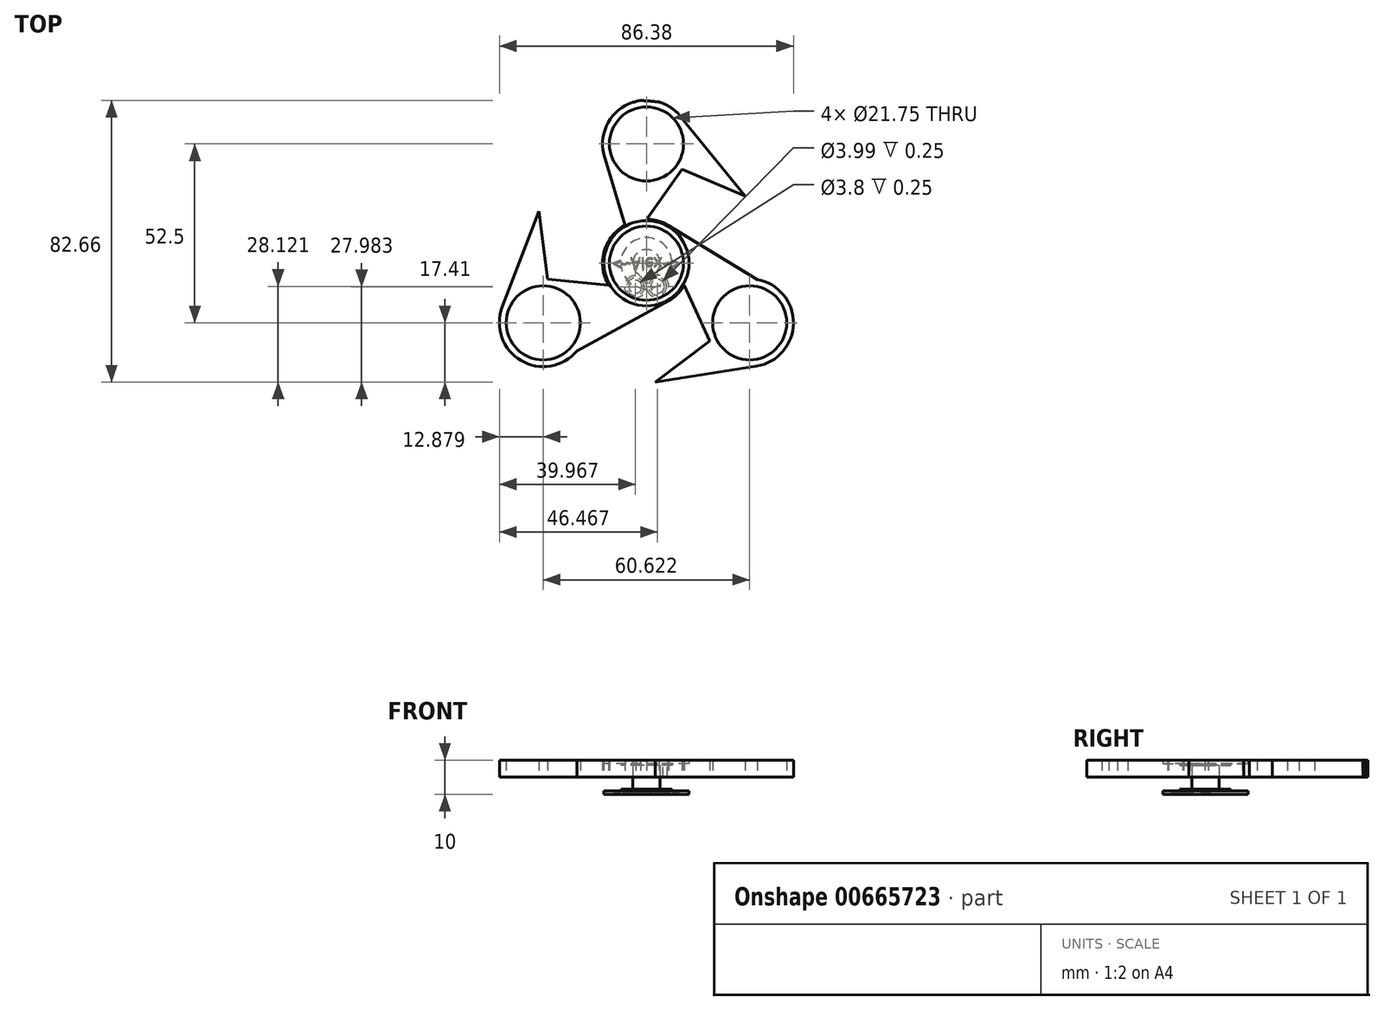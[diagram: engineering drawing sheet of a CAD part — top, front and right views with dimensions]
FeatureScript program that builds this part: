
annotation { "Feature Type Name" : "Feature", "Feature Type Description" : "" }
export const myFeature = defineFeature(function(context is Context, id is Id, definition is map)
    precondition{}
    {
        {
            var Q0;
            Q0=qCreatedBy(makeId("Top.planeOp"),FACE);
            var sketch = newSketch(context, id + "F0", { "sketchPlane" : qUnion([Q0])});
            skCircle(sketch, "E0", {"center": v(0, 0) * mm, "radius": 11.1 * mm});
            skCircle(sketch, "E1", {"center": v(0, 0) * mm, "radius": 4 * mm});
            skCircle(sketch, "E2.cCircle", {"center": v(0, 24.15) * mm, "radius": 6.8 * mm, "construction": true});
            skLineSegment(sketch, "E2.0", {"start": v(3.93, 17.35) * mm, "end": v(-3.93, 17.35) * mm});
            skLineSegment(sketch, "E2.1", {"start": v(-3.93, 17.35) * mm, "end": v(-7.85, 24.15) * mm});
            skLineSegment(sketch, "E2.2", {"start": v(-7.85, 24.15) * mm, "end": v(-3.93, 30.95) * mm});
            skLineSegment(sketch, "E2.3", {"start": v(-3.93, 30.95) * mm, "end": v(3.93, 30.95) * mm});
            skLineSegment(sketch, "E2.4", {"start": v(3.93, 30.95) * mm, "end": v(7.85, 24.15) * mm});
            skLineSegment(sketch, "E2.5", {"start": v(7.85, 24.15) * mm, "end": v(3.93, 17.35) * mm});
            skPoint(sketch, "E2.0.midPoint", {"position": v(0, 17.35) * mm});
            skLineSegment(sketch, "E3", {"start": v(0, 0) * mm, "end": v(0, 35) * mm, "construction": true});
            skArc(sketch, "E4", {"start": v(-11.18, 8.6) * mm, "mid": v(-12.21, 7.05) * mm, "end": v(-13.03, 5.38) * mm});
            skArc(sketch, "E5", {"start": v(-11.18, 8.6) * mm, "mid": v(-9, 13.96) * mm, "end": v(-9.89, 19.68) * mm});
            skArc(sketch, "E6", {"start": v(9.89, 19.68) * mm, "mid": v(9, 13.96) * mm, "end": v(11.18, 8.6) * mm});
            skArc(sketch, "E7.trimOffspring", {"start": v(9.89, 19.68) * mm, "mid": v(0, 35) * mm, "end": v(-9.89, 19.68) * mm});
            skArc(sketch, "E8.1.0", {"start": v(-1.86, -13.98) * mm, "mid": v(-7.59, -14.77) * mm, "end": v(-12.1, -18.4) * mm});
            skArc(sketch, "E8.1.1", {"start": v(-21.99, -1.28) * mm, "mid": v(-30.31, -17.5) * mm, "end": v(-12.1, -18.4) * mm});
            skLineSegment(sketch, "E8.1.2", {"start": v(-13.06, -12.07) * mm, "end": v(-16.99, -18.87) * mm});
            skLineSegment(sketch, "E8.1.3", {"start": v(-16.99, -18.87) * mm, "end": v(-24.84, -18.87) * mm});
            skLineSegment(sketch, "E8.1.4", {"start": v(-24.84, -18.87) * mm, "end": v(-28.76, -12.07) * mm});
            skLineSegment(sketch, "E8.1.5", {"start": v(-28.76, -12.07) * mm, "end": v(-24.84, -5.27) * mm});
            skLineSegment(sketch, "E8.1.6", {"start": v(-24.84, -5.27) * mm, "end": v(-16.99, -5.27) * mm});
            skLineSegment(sketch, "E8.1.7", {"start": v(-16.99, -5.27) * mm, "end": v(-13.06, -12.07) * mm});
            skArc(sketch, "E8.1.8", {"start": v(-21.99, -1.28) * mm, "mid": v(-16.59, 0.81) * mm, "end": v(-13.03, 5.38) * mm});
            skArc(sketch, "E8.2.0", {"start": v(13.03, 5.38) * mm, "mid": v(16.59, 0.81) * mm, "end": v(21.99, -1.28) * mm});
            skArc(sketch, "E8.2.1", {"start": v(12.1, -18.4) * mm, "mid": v(30.31, -17.5) * mm, "end": v(21.99, -1.28) * mm});
            skLineSegment(sketch, "E8.2.2", {"start": v(16.99, -5.27) * mm, "end": v(24.84, -5.27) * mm});
            skLineSegment(sketch, "E8.2.3", {"start": v(24.84, -5.27) * mm, "end": v(28.76, -12.07) * mm});
            skLineSegment(sketch, "E8.2.4", {"start": v(28.76, -12.07) * mm, "end": v(24.84, -18.87) * mm});
            skLineSegment(sketch, "E8.2.5", {"start": v(24.84, -18.87) * mm, "end": v(16.99, -18.87) * mm});
            skLineSegment(sketch, "E8.2.6", {"start": v(16.99, -18.87) * mm, "end": v(13.06, -12.07) * mm});
            skLineSegment(sketch, "E8.2.7", {"start": v(13.06, -12.07) * mm, "end": v(16.99, -5.27) * mm});
            skArc(sketch, "E8.2.8", {"start": v(12.1, -18.4) * mm, "mid": v(7.59, -14.77) * mm, "end": v(1.86, -13.98) * mm});
            skArc(sketch, "E9.trimOffspring", {"start": v(-1.86, -13.98) * mm, "mid": v(0, -14.1) * mm, "end": v(1.86, -13.98) * mm});
            skArc(sketch, "E10.trimOffspring", {"start": v(13.03, 5.38) * mm, "mid": v(12.21, 7.05) * mm, "end": v(11.18, 8.6) * mm});
            skArc(sketch, "E11", {"start": v(-13.03, 5.38) * mm, "mid": v(-14.09, 0.64) * mm, "end": v(-13.47, -4.18) * mm});
            skArc(sketch, "E12", {"start": v(11.18, 8.6) * mm, "mid": v(7.6, 11.88) * mm, "end": v(3.11, 13.75) * mm});
            skArc(sketch, "E13", {"start": v(1.86, -13.98) * mm, "mid": v(6.49, -12.52) * mm, "end": v(10.35, -9.57) * mm});
            skArc(sketch, "E14", {"start": v(-12.1, -18.4) * mm, "mid": v(-10.27, -14.18) * mm, "end": v(-10.35, -9.57) * mm});
            skArc(sketch, "E15", {"start": v(-9.89, 19.68) * mm, "mid": v(-7.14, 15.98) * mm, "end": v(-3.11, 13.75) * mm});
            skArc(sketch, "E16", {"start": v(21.99, -1.28) * mm, "mid": v(17.41, -1.8) * mm, "end": v(13.47, -4.18) * mm});
            skLineSegment(sketch, "E17", {"start": v(0, 24.15) * mm, "end": v(5.43, 33.55) * mm, "construction": true});
            skArc(sketch, "E18.trimOffspring", {"start": v(-13.47, -4.18) * mm, "mid": v(-17.41, -1.8) * mm, "end": v(-21.99, -1.28) * mm});
            skArc(sketch, "E19.trimOffspring", {"start": v(10.35, -9.57) * mm, "mid": v(10.27, -14.18) * mm, "end": v(12.1, -18.4) * mm});
            skArc(sketch, "E20.trimOffspring", {"start": v(3.11, 13.75) * mm, "mid": v(7.14, 15.98) * mm, "end": v(9.89, 19.68) * mm});
            skCircle(sketch, "E21", {"center": v(0, 0) * mm, "radius": 7.5 * mm});
            skCircle(sketch, "E22", {"center": v(0, 0) * mm, "radius": 12.5 * mm});
            skArc(sketch, "E23.trimOffspring", {"start": v(-3.11, 13.75) * mm, "mid": v(-7.6, 11.88) * mm, "end": v(-11.18, 8.6) * mm});
            skArc(sketch, "E24.trimOffspring", {"start": v(-10.35, -9.57) * mm, "mid": v(-6.49, -12.52) * mm, "end": v(-1.86, -13.98) * mm});
            skArc(sketch, "E25.trimOffspring", {"start": v(13.47, -4.18) * mm, "mid": v(14.09, 0.64) * mm, "end": v(13.03, 5.38) * mm});
            skSolve(sketch);
        }
        {
            var Q0;
            {var subQ1=sQuery(id+"F0.wireOp",EDGE,"E8.1.1");Q0=makeQuery(id+"F0.imprint","IMPRINT",FACE,{"disambiguationData":[TD([[makeQuery(id+"F0.imprint","IMPRINT",EDGE,{"derivedFrom":subQ1}),1.0]])]});}
            var Q1;
            {var subQ0=sQuery(id+"F0.wireOp",EDGE,"E8.1.8");Q1=makeQuery(id+"F0.imprint","IMPRINT",FACE,{"disambiguationData":[TD([[makeQuery(id+"F0.imprint","IMPRINT",EDGE,{"derivedFrom":subQ0}),-1.0]])]});}
            var Q2;
            Q2=makeQuery(id+"F0.imprint","IMPRINT",FACE,{"disambiguationData":[TD([[makeQuery(id+"F0.imprint","IMPRINT",EDGE,{"derivedFrom":sQuery(id+"F0.wireOp",EDGE,"E0")}),-1.0]])]});
            var Q3;
            {var subQ0=sQuery(id+"F0.wireOp",EDGE,"E5");Q3=makeQuery(id+"F0.imprint","IMPRINT",FACE,{"disambiguationData":[TD([[makeQuery(id+"F0.imprint","IMPRINT",EDGE,{"derivedFrom":subQ0}),-1.0]])]});}
            var Q4;
            Q4=makeQuery(id+"F0.imprint","IMPRINT",FACE,{"disambiguationData":[TD([[makeQuery(id+"F0.imprint","IMPRINT",EDGE,{"derivedFrom":sQuery(id+"F0.wireOp",EDGE,"E2.0")}),1.0]])]});
            var Q5;
            {var subQ0=sQuery(id+"F0.wireOp",EDGE,"E8.1.0");Q5=makeQuery(id+"F0.imprint","IMPRINT",FACE,{"disambiguationData":[TD([[makeQuery(id+"F0.imprint","IMPRINT",EDGE,{"derivedFrom":subQ0}),-1.0]])]});}
            var Q6;
            {var subQ0=sQuery(id+"F0.wireOp",EDGE,"E8.2.0");Q6=makeQuery(id+"F0.imprint","IMPRINT",FACE,{"disambiguationData":[TD([[makeQuery(id+"F0.imprint","IMPRINT",EDGE,{"derivedFrom":subQ0}),-1.0]])]});}
            var Q7;
            {var subQ0=sQuery(id+"F0.wireOp",EDGE,"E8.2.8");Q7=makeQuery(id+"F0.imprint","IMPRINT",FACE,{"disambiguationData":[TD([[makeQuery(id+"F0.imprint","IMPRINT",EDGE,{"derivedFrom":subQ0}),-1.0]])]});}
            var Q8;
            {var subQ0=sQuery(id+"F0.wireOp",EDGE,"E8.2.1");Q8=makeQuery(id+"F0.imprint","IMPRINT",FACE,{"disambiguationData":[TD([[makeQuery(id+"F0.imprint","IMPRINT",EDGE,{"derivedFrom":subQ0}),1.0]])]});}
            var Q9;
            {var subQ0=sQuery(id+"F0.wireOp",EDGE,"E6");Q9=makeQuery(id+"F0.imprint","IMPRINT",FACE,{"disambiguationData":[TD([[makeQuery(id+"F0.imprint","IMPRINT",EDGE,{"derivedFrom":subQ0}),-1.0]])]});}
            var Q10;
            {var subQ4=sQuery(id+"F0.wireOp",EDGE,"E4");Q10=makeQuery(id+"F0.imprint","IMPRINT",FACE,{"disambiguationData":[TD([[makeQuery(id+"F0.imprint","IMPRINT",EDGE,{"derivedFrom":subQ4}),1.0]])]});}
            extrude(context, id + "F1", {"entities" : qUnion([Q0, Q1, Q2, Q3, Q4, Q5, Q6, Q7, Q8, Q9, Q10]), "endBound" : BoundingType.SYMMETRIC, "depth" : 3 * mm, "offsetDistance" : 25 * mm});
        }
        {
            var Q0;
            Q0=makeQuery(id+"F0.imprint","IMPRINT",FACE,{"disambiguationData":[TD([[makeQuery(id+"F0.imprint","IMPRINT",EDGE,{"derivedFrom":sQuery(id+"F0.wireOp",EDGE,"E0")}),-1.0]])]});
            var Q1;
            Q1=makeQuery(id+"F0.imprint","IMPRINT",FACE,{"disambiguationData":[TD([[makeQuery(id+"F0.imprint","IMPRINT",EDGE,{"derivedFrom":sQuery(id+"F0.wireOp",EDGE,"E2.0")}),1.0]])]});
            extrude(context, id + "F2", {"entities" : qUnion([Q0, Q1]), "operationType" : NewBodyOperationType.ADD, "endBound" : BoundingType.SYMMETRIC, "oppositeDirection" : true, "depth" : 7 * mm, "offsetDistance" : 25 * mm});
        }
        {
            var Q0;
            Q0=makeQuery(id+"F0.imprint","IMPRINT",FACE,{"disambiguationData":[TD([[makeQuery(id+"F0.imprint","IMPRINT",EDGE,{"derivedFrom":sQuery(id+"F0.wireOp",EDGE,"E1")}),1.0]])]});
            extrude(context, id + "F3", {"entities" : qUnion([Q0]), "depth" : 3.5 * mm, "offsetDistance" : 25 * mm});
        }
        {
            var Q0;
            Q0=makeQuery(id+"F0.imprint","IMPRINT",FACE,{"disambiguationData":[TD([[makeQuery(id+"F0.imprint","IMPRINT",EDGE,{"derivedFrom":sQuery(id+"F0.wireOp",EDGE,"E1")}),1.0]])]});
            var Q1;
            Q1=makeQuery(id+"F0.imprint","IMPRINT",FACE,{"disambiguationData":[TD([[makeQuery(id+"F0.imprint","IMPRINT",EDGE,{"derivedFrom":sQuery(id+"F0.wireOp",EDGE,"E1")}),-1.0]])]});
            var Q2;
            Q2=makeQuery(id+"F3.opExtrude","CAP_FACE",FACE,{"disambiguationData":[OSD([sQuery(id+"F0.wireOp",EDGE,"E1")])],"isStart":false});
            extrude(context, id + "F4", {"entities" : qUnion([Q0, Q1]), "operationType" : NewBodyOperationType.ADD, "depth" : 4 * mm, "offsetDistance" : 25 * mm, "hasSecondDirection" : true, "secondDirectionBound" : SecondDirectionBoundingType.UP_TO_SURFACE, "secondDirectionOppositeDirection" : false, "secondDirectionDepth" : 25 * mm, "secondDirectionBoundEntityFace" : qUnion([Q2])});
        }
        {
            var Q0;
            Q0=makeQuery(id+"F0.imprint","IMPRINT",FACE,{"disambiguationData":[TD([[makeQuery(id+"F0.imprint","IMPRINT",EDGE,{"derivedFrom":sQuery(id+"F0.wireOp",EDGE,"E0")}),-1.0]])]});
            var Q1;
            Q1=makeQuery(id+"F0.imprint","IMPRINT",FACE,{"disambiguationData":[TD([[makeQuery(id+"F0.imprint","IMPRINT",EDGE,{"derivedFrom":sQuery(id+"F0.wireOp",EDGE,"E0")}),1.0]])]});
            var Q2;
            Q2=makeQuery(id+"F0.imprint","IMPRINT",FACE,{"disambiguationData":[TD([[makeQuery(id+"F0.imprint","IMPRINT",EDGE,{"derivedFrom":sQuery(id+"F0.wireOp",EDGE,"E1")}),-1.0]])]});
            var Q3;
            Q3=makeQuery(id+"F0.imprint","IMPRINT",FACE,{"disambiguationData":[TD([[makeQuery(id+"F0.imprint","IMPRINT",EDGE,{"derivedFrom":sQuery(id+"F0.wireOp",EDGE,"E1")}),1.0]])]});
            var Q4;
            Q4=makeQuery(id+"F4.opExtrude","CAP_FACE",FACE,{"disambiguationData":[OSD([sQuery(id+"F0.wireOp",EDGE,"E21")])],"isStart":false});
            extrude(context, id + "F5", {"entities" : qUnion([Q0, Q1, Q2, Q3]), "operationType" : NewBodyOperationType.ADD, "depth" : 5 * mm, "offsetDistance" : 25 * mm, "hasSecondDirection" : true, "secondDirectionBound" : SecondDirectionBoundingType.UP_TO_SURFACE, "secondDirectionOppositeDirection" : false, "secondDirectionDepth" : 25 * mm, "secondDirectionBoundEntityFace" : qUnion([Q4])});
        }
        {
            var Q0;
            Q0=makeQuery(id+"F3.opExtrude","SWEPT_BODY",BODY,{"disambiguationData":[OSD([sQuery(id+"F0.wireOp",EDGE,"E1")])]});
            var Q1;
            Q1=makeQuery(id+"F3.opExtrude","CAP_FACE",FACE,{"disambiguationData":[OSD([sQuery(id+"F0.wireOp",EDGE,"E1")])],"isStart":true});
            mirror(context, id + "F6", {"entities" : qUnion([Q0]), "mirrorPlane" : qUnion([Q1])});
        }
        {
            var Q0;
            Q0=makeQuery(id+"F6.opPattern","COPY",FACE,{"derivedFrom":makeQuery(id+"F5.opExtrude","CAP_FACE",FACE,{"disambiguationData":[OSD([sQuery(id+"F0.wireOp",EDGE,"E22")])],"isStart":false}),"instanceName":"1"});
            var sketch = newSketch(context, id + "F7", { "sketchPlane" : qUnion([Q0])});
            skText(sketch, "E26", { "text": "<~Alex~>", "fontName": "OpenSans-Regular.ttf"});
            skPoint(sketch, "E27", {"position": v(0, -12.5) * mm});
            skPoint(sketch, "E28", {"position": v(-12.5, 0) * mm});
            const initialGuessF7  = {"E26": [-0.01, -0.0015, 1, 0, 0.00337]};
            skSetInitialGuess(sketch, initialGuessF7);
            skSolve(sketch);
        }
        {
            var Q0;
            Q0=makeQuery(id+"F7.imprint","IMPRINT",FACE,{"disambiguationData":[TD([[makeQuery(id+"F7.imprint","IMPRINT",EDGE,{"derivedFrom":sQuery(id+"F7.wireOp",EDGE,"E26.sketch_text.stroke-0")}),1.0]])]});
            var sketch = newSketch(context, id + "F8", { "sketchPlane" : qUnion([Q0])});
            skArc(sketch, "E29", {"start": v(0.04, 6.25) * mm, "mid": v(6.55, 6.67) * mm, "end": v(0.1, 7.57) * mm});
            skPoint(sketch, "E30.center.orphan", {"position": v(0, 6.93) * mm});
            skCircle(sketch, "E31", {"center": v(-3.22, 6.93) * mm, "radius": 2.57 * mm});
            skCircle(sketch, "E32", {"center": v(3.28, 6.79) * mm, "radius": 2.62 * mm});
            skLineSegment(sketch, "E33.trimOffspring", {"start": v(-0.07, 7.62) * mm, "end": v(-0.07, 7.62) * mm});
            skPoint(sketch, "E34.1.internal.orphan", {"position": v(0.1, 7.15) * mm});
            skArc(sketch, "E35", {"start": v(-0.07, 7.62) * mm, "mid": v(-6.45, 6.97) * mm, "end": v(-0.1, 6.14) * mm});
            skFitSpline(sketch, "E36", {"points": [v(-0.07, 7.62) * mm, v(0, 7.34) * mm, v(0.1, 7.57) * mm, v(0.3, 7.07) * mm, v(0.3, 6.56) * mm, v(0.3, 6.34) * mm], "startDerivative": vector(0.4, -2.54) * mm, "endDerivative": vector(0.05, -1.27) * mm});
            skFitSpline(sketch, "E37", {"points": [v(-0.1, 6.14) * mm, v(0, 6.43) * mm, v(0.04, 6.25) * mm], "startDerivative": vector(0.2, 0.78) * mm, "endDerivative": vector(0.08, -0.63) * mm});
            skPoint(sketch, "E38.3.internal.orphan", {"position": v(0.04, 6.93) * mm});
            skPoint(sketch, "E38.4.internal.orphan", {"position": v(-0.1, 7.15) * mm});
            skPoint(sketch, "E38.endDerivative.orphan", {"position": v(0.3, 6.89) * mm});
            skCircle(sketch, "E39", {"center": v(-3.22, 6.93) * mm, "radius": 1.9 * mm});
            skCircle(sketch, "E40", {"center": v(3.28, 6.79) * mm, "radius": 2 * mm});
            skLineSegment(sketch, "E41", {"start": v(-12.67, 0) * mm, "end": v(21.78, 0) * mm});
            skLineSegment(sketch, "E42", {"start": v(21.78, 0) * mm, "end": v(16.86, 11.11) * mm});
            skArc(sketch, "E43.MirrorCS", {"start": v(0.04, -6.25) * mm, "mid": v(6.55, -6.67) * mm, "end": v(0.1, -7.57) * mm});
            skArc(sketch, "E44.MirrorCS", {"start": v(-0.07, -7.62) * mm, "mid": v(-6.45, -6.97) * mm, "end": v(-0.1, -6.14) * mm});
            skCircle(sketch, "E45.MirrorC", {"center": v(-3.22, -6.93) * mm, "radius": 2.57 * mm});
            skCircle(sketch, "E46.MirrorC", {"center": v(-3.22, -6.93) * mm, "radius": 1.9 * mm});
            skCircle(sketch, "E47.MirrorC", {"center": v(3.28, -6.79) * mm, "radius": 2 * mm});
            skCircle(sketch, "E48.MirrorC", {"center": v(3.28, -6.79) * mm, "radius": 2.62 * mm});
            skFitSpline(sketch, "E49.MirrorCS", {"points": [v(-0.1, -6.14) * mm, v(0, -6.43) * mm, v(0.04, -6.25) * mm], "startDerivative": vector(0.2, -0.78) * mm, "endDerivative": vector(0.08, 0.63) * mm});
            skFitSpline(sketch, "E50.MirrorCS", {"points": [v(-0.07, -7.62) * mm, v(0, -7.34) * mm, v(0.1, -7.57) * mm, v(0.3, -7.07) * mm, v(0.3, -6.56) * mm, v(0.3, -6.34) * mm], "startDerivative": vector(0.4, 2.54) * mm, "endDerivative": vector(0.05, 1.27) * mm});
            skSolve(sketch);
        }
        {
            var Q0;
            Q0=makeQuery(id+"F8.imprint","IMPRINT",FACE,{"disambiguationData":[TD([[makeQuery(id+"F8.imprint","IMPRINT",EDGE,{"derivedFrom":sQuery(id+"F8.wireOp",EDGE,"E40")}),1.0]])]});
            var Q1;
            Q1=makeQuery(id+"F8.imprint","IMPRINT",FACE,{"disambiguationData":[TD([[makeQuery(id+"F8.imprint","IMPRINT",EDGE,{"derivedFrom":sQuery(id+"F8.wireOp",EDGE,"E29")}),1.0]])]});
            var Q2;
            Q2=makeQuery(id+"F8.imprint","IMPRINT",FACE,{"disambiguationData":[TD([[makeQuery(id+"F8.imprint","IMPRINT",EDGE,{"derivedFrom":sQuery(id+"F8.wireOp",EDGE,"E39")}),1.0]])]});
            extrude(context, id + "F9", {"entities" : qUnion([Q0, Q1, Q2]), "operationType" : NewBodyOperationType.REMOVE, "oppositeDirection" : true, "depth" : .25 * mm, "offsetDistance" : 25 * mm});
        }
        {
            var Q0;
            Q0=qSketchRegion(id+"F7",true);
            extrude(context, id + "F10", {"entities" : qUnion([Q0]), "operationType" : NewBodyOperationType.REMOVE, "oppositeDirection" : true, "depth" : .25 * mm, "offsetDistance" : 25 * mm});
        }
        {
            var Q0;
            Q0=qCreatedBy(makeId("Top.planeOp"),FACE);
            var sketch = newSketch(context, id + "F11", { "sketchPlane" : qUnion([Q0])});
            skFitSpline(sketch, "E51", {"points": [v(10.44, 24.14) * mm, v(8.47, 14.54) * mm, v(13.87, 0) * mm, v(17.82, 0) * mm, v(24.67, 0) * mm, v(31.02, -10.75) * mm, v(30.16, -18.9) * mm, v(23.73, -20.7) * mm, v(14.13, -19.32) * mm, v(11.82, -16.15) * mm, v(8.13, -13.24) * mm, v(0, -13.15) * mm, v(-10.47, -13.58) * mm, v(-14.93, -19.32) * mm, v(-25.56, -20.35) * mm, v(-29.93, -11.44) * mm, v(-26.08, -4.06) * mm, v(-15.96, 0) * mm, v(-7.39, 13.94) * mm, v(-9.62, 23.97) * mm, v(-4.73, 32.28) * mm, v(0, 32.71) * mm, v(5.9, 32.2) * mm, v(10.44, 24.14) * mm]});
            skFitSpline(sketch, "E52", {"points": [v(-15.81, 42.22) * mm, v(51.8, 40.54) * mm, v(46.07, -43.82) * mm, v(-39.37, -51.4) * mm, v(-45.4, 26.76) * mm, v(-15.81, 42.22) * mm]});
            skSolve(sketch);
        }
        {
            var Q0;
            Q0=makeQuery(id+"F11.imprint","IMPRINT",FACE,{"disambiguationData":[TD([[makeQuery(id+"F11.imprint","IMPRINT",EDGE,{"derivedFrom":sQuery(id+"F11.wireOp",EDGE,"E51")}),1.0]])]});
            extrude(context, id + "F12", {"entities" : qUnion([Q0]), "operationType" : NewBodyOperationType.ADD, "depth" : 3.5 * mm, "offsetDistance" : 25 * mm, "hasSecondDirection" : true, "secondDirectionOppositeDirection" : true, "secondDirectionDepth" : 3.5 * mm});
        }
        {
            var Q0;
            Q0=qCreatedBy(makeId("Top.planeOp"),FACE);
            var sketch = newSketch(context, id + "F13", { "sketchPlane" : qUnion([Q0])});
            skFitSpline(sketch, "E53", {"points": [v(-25.09, 0) * mm, v(-14.35, -5.2) * mm, v(-11.22, -15.94) * mm, v(0, -23.88) * mm, v(7.56, -22.09) * mm, v(12.03, -9.9) * mm, v(16.62, -3.98) * mm, v(28.36, -5.32) * mm, v(30.48, -14.7) * mm, v(25.23, -20.86) * mm, v(37.64, -20.52) * mm], "startDerivative": vector(125.02, -33) * mm, "endDerivative": vector(170.09, 21.27) * mm});
            skFitSpline(sketch, "E54", {"points": [v(-13.12, 7.76) * mm, v(-10.1, -5.2) * mm, v(0, -15.94) * mm, v(12.03, -5.2) * mm, v(12.03, 0) * mm, v(12.03, 7.54) * mm, v(0, 11.34) * mm, v(-13.12, 7.76) * mm]});
            skPoint(sketch, "E55.1.internal.orphan", {"position": v(42, 0) * mm});
            skPoint(sketch, "E55.5.internal.orphan", {"position": v(0, 15.48) * mm});
            skFitSpline(sketch, "E56", {"points": [v(-25.09, 0) * mm, v(-18.56, 21.41) * mm, v(0, 15.48) * mm, v(16.77, 30.45) * mm, v(42, 0) * mm, v(37.64, -20.52) * mm], "startDerivative": vector(12.87, 163.32) * mm, "endDerivative": vector(-53.42, -92.17) * mm});
            skSolve(sketch);
        }
        {
            var Q0;
            Q0=qSketchRegion(id+"F13",true);
            extrude(context, id + "F14", {"entities" : qUnion([Q0]), "operationType" : NewBodyOperationType.ADD, "depth" : 3.5 * mm, "offsetDistance" : 25 * mm, "hasSecondDirection" : true, "secondDirectionOppositeDirection" : true, "secondDirectionDepth" : 3.5 * mm});
        }
        {
            var Q0;
            Q0=qCreatedBy(makeId("Top.planeOp"),FACE);
            var sketch = newSketch(context, id + "F15", { "sketchPlane" : qUnion([Q0])});
            skFitSpline(sketch, "E57", {"points": [v(2.61, -14.25) * mm, v(8.47, -15.43) * mm, v(8.17, -10.3) * mm, v(2.61, -14.25) * mm]});
            skSolve(sketch);
        }
        {
            var Q0;
            Q0=qSketchRegion(id+"F15",true);
            extrude(context, id + "F16", {"entities" : qUnion([Q0]), "operationType" : NewBodyOperationType.ADD, "depth" : 3.5 * mm, "offsetDistance" : 25 * mm, "hasSecondDirection" : true, "secondDirectionOppositeDirection" : true, "secondDirectionDepth" : 3.5 * mm});
        }
        {
            var Q0;
            Q0=qCreatedBy(makeId("Top.planeOp"),FACE);
            var sketch = newSketch(context, id + "F17", { "sketchPlane" : qUnion([Q0])});
            skCircle(sketch, "E58", {"center": v(0, 0) * mm, "radius": 43.92 * mm});
            skCircle(sketch, "E59", {"center": v(0, 0) * mm, "radius": 70.15 * mm});
            skSolve(sketch);
        }
        {
            var Q0;
            Q0=qSketchRegion(id+"F17",true);
            extrude(context, id + "F18", {"entities" : qUnion([Q0]), "operationType" : NewBodyOperationType.REMOVE, "oppositeDirection" : true, "depth" : 25 * mm, "offsetDistance" : 25 * mm, "hasSecondDirection" : true, "secondDirectionOppositeDirection" : false, "secondDirectionDepth" : 25 * mm});
        }
        {
            var Q0;
            Q0=makeQuery(id+"F1.opExtrude","SWEPT_BODY",BODY,{"disambiguationData":[OSD([sQuery(id+"F0.wireOp",EDGE,"E0"),sQuery(id+"F0.wireOp",EDGE,"E2.0"),sQuery(id+"F0.wireOp",EDGE,"E2.1"),sQuery(id+"F0.wireOp",EDGE,"E2.2"),sQuery(id+"F0.wireOp",EDGE,"E2.3"),sQuery(id+"F0.wireOp",EDGE,"E2.4"),sQuery(id+"F0.wireOp",EDGE,"E2.5"),sQuery(id+"F0.wireOp",EDGE,"E4"),sQuery(id+"F0.wireOp",EDGE,"E5"),sQuery(id+"F0.wireOp",EDGE,"E6"),sQuery(id+"F0.wireOp",EDGE,"E7.trimOffspring"),sQuery(id+"F0.wireOp",EDGE,"E8.1.0"),sQuery(id+"F0.wireOp",EDGE,"E8.1.1"),sQuery(id+"F0.wireOp",EDGE,"E8.1.2"),sQuery(id+"F0.wireOp",EDGE,"E8.1.3"),sQuery(id+"F0.wireOp",EDGE,"E8.1.4"),sQuery(id+"F0.wireOp",EDGE,"E8.1.5"),sQuery(id+"F0.wireOp",EDGE,"E8.1.6"),sQuery(id+"F0.wireOp",EDGE,"E8.1.7"),sQuery(id+"F0.wireOp",EDGE,"E8.1.8"),sQuery(id+"F0.wireOp",EDGE,"E8.2.0"),sQuery(id+"F0.wireOp",EDGE,"E8.2.1"),sQuery(id+"F0.wireOp",EDGE,"E8.2.2"),sQuery(id+"F0.wireOp",EDGE,"E8.2.3"),sQuery(id+"F0.wireOp",EDGE,"E8.2.4"),sQuery(id+"F0.wireOp",EDGE,"E8.2.5"),sQuery(id+"F0.wireOp",EDGE,"E8.2.6"),sQuery(id+"F0.wireOp",EDGE,"E8.2.7"),sQuery(id+"F0.wireOp",EDGE,"E8.2.8"),sQuery(id+"F0.wireOp",EDGE,"E9.trimOffspring"),sQuery(id+"F0.wireOp",EDGE,"E10.trimOffspring")])]});
            deleteBodies(context, id + "F19", {"entities" : qUnion([Q0])});
        }
        {
            var Q0;
            Q0=qCreatedBy(makeId("Top.planeOp"),FACE);
            var sketch = newSketch(context, id + "F20", { "sketchPlane" : qUnion([Q0])});
            skCircle(sketch, "E60", {"center": v(0, 0) * mm, "radius": 62.5 * mm});
            skCircle(sketch, "E61", {"center": v(0, 0) * mm, "radius": 10.88 * mm});
            skCircle(sketch, "E62", {"center": v(0, 35) * mm, "radius": 10.88 * mm});
            skCircle(sketch, "E63.1.0", {"center": v(-30.31, -17.5) * mm, "radius": 10.88 * mm});
            skCircle(sketch, "E63.2.0", {"center": v(30.31, -17.5) * mm, "radius": 10.88 * mm});
            skCircle(sketch, "E64", {"center": v(0, 35) * mm, "radius": 12.88 * mm});
            skCircle(sketch, "E65", {"center": v(0, 0) * mm, "radius": 12.88 * mm});
            skCircle(sketch, "E66.1.0", {"center": v(-30.31, -17.5) * mm, "radius": 12.88 * mm});
            skCircle(sketch, "E66.2.0", {"center": v(30.31, -17.5) * mm, "radius": 12.88 * mm});
            skPoint(sketch, "E67.end.orphan", {"position": v(-3.97, 22.75) * mm});
            skPoint(sketch, "E67.start.orphan", {"position": v(-6.3, 11.22) * mm});
            skPoint(sketch, "E68.MirrorCS.end.orphan", {"position": v(3.97, 22.75) * mm});
            skPoint(sketch, "E68.MirrorCS.start.orphan", {"position": v(6.3, 11.22) * mm});
            skFitSpline(sketch, "E69", {"points": [v(-16.24, 32.05) * mm, v(-11.42, 45.17) * mm, v(-3.1, 47.5) * mm, v(-6.43, 48.7) * mm], "startDerivative": vector(3.39, 36.93) * mm, "endDerivative": vector(-23.98, 6.34) * mm});
            skPoint(sketch, "E70.orphan", {"position": v(-11.42, 40.94) * mm});
            skFitSpline(sketch, "E71", {"points": [v(-16.24, 32.05) * mm, v(-11.42, 45.17) * mm, v(-6.43, 48.7) * mm, v(0, 48.7) * mm, v(6.12, 46.33) * mm], "startDerivative": vector(12.47, 46.03) * mm, "endDerivative": vector(26.23, -12.53) * mm});
            skPoint(sketch, "E72.1.internal.orphan", {"position": v(-16.26, 22.75) * mm});
            skFitSpline(sketch, "E73", {"points": [v(-12.87, -0.15) * mm, v(-16.26, 22.75) * mm, v(-11.42, 45.17) * mm, v(4.14, 47.27) * mm], "startDerivative": vector(-12.88, 60.7) * mm, "endDerivative": vector(61.47, -6.4) * mm});
            skFitSpline(sketch, "E74", {"points": [v(-6.3, 11.22) * mm, v(-12.53, 32.05) * mm], "startDerivative": vector(-6.22, 20.82) * mm, "endDerivative": vector(-6.22, 20.82) * mm});
            skLineSegment(sketch, "E75", {"start": v(-12.87, -0.15) * mm, "end": v(-12.1, 30.6) * mm});
            skLineSegment(sketch, "E76.1.0", {"start": v(6.56, -11.08) * mm, "end": v(-20.45, -25.77) * mm});
            skLineSegment(sketch, "E76.2.0", {"start": v(6.3, 11.22) * mm, "end": v(32.54, -4.82) * mm});
            skLineSegment(sketch, "E77", {"start": v(0, 12.88) * mm, "end": v(10.47, 27.5) * mm});
            skLineSegment(sketch, "E78.1.0", {"start": v(-11.15, -6.44) * mm, "end": v(-29.06, -4.69) * mm});
            skLineSegment(sketch, "E78.2.0", {"start": v(11.15, -6.44) * mm, "end": v(18.59, -22.82) * mm});
            skPoint(sketch, "E79.end.orphan", {"position": v(26.57, 27.5) * mm});
            skPoint(sketch, "E79.start.orphan", {"position": v(10.47, 42.5) * mm});
            skPoint(sketch, "E80.orphan", {"position": v(-29.06, -4.69) * mm});
            skPoint(sketch, "E81.orphan", {"position": v(18.59, -22.82) * mm});
            skLineSegment(sketch, "E82", {"start": v(-29.06, -4.69) * mm, "end": v(-31.52, 15.22) * mm});
            skLineSegment(sketch, "E83", {"start": v(-31.52, 15.22) * mm, "end": v(-42.33, -12.88) * mm});
            skArc(sketch, "E84.trimOffspring", {"start": v(-31.52, 15.22) * mm, "mid": v(-32.67, 12.57) * mm, "end": v(-33.6, 9.83) * mm});
            skLineSegment(sketch, "E85.1.0", {"start": v(2.58, -34.9) * mm, "end": v(32.32, -30.22) * mm});
            skLineSegment(sketch, "E85.1.1", {"start": v(18.59, -22.82) * mm, "end": v(2.58, -34.9) * mm});
            skLineSegment(sketch, "E85.2.0", {"start": v(28.94, 19.68) * mm, "end": v(10.01, 43.1) * mm});
            skLineSegment(sketch, "E85.2.1", {"start": v(10.47, 27.5) * mm, "end": v(28.94, 19.68) * mm});
            skSolve(sketch);
        }
        {
            var Q0;
            Q0=makeQuery(id+"F20.imprint","IMPRINT",FACE,{"disambiguationData":[TD([[makeQuery(id+"F20.imprint","IMPRINT",EDGE,{"derivedFrom":sQuery(id+"F20.wireOp",EDGE,"E62")}),-1.0]])]});
            var Q1;
            {var subQ3=sQuery(id+"F20.wireOp",EDGE,"E77");Q1=makeQuery(id+"F20.imprint","IMPRINT",FACE,{"disambiguationData":[TD([[makeQuery(id+"F20.imprint","IMPRINT",EDGE,{"derivedFrom":subQ3}),1.0]])]});}
            var Q2;
            Q2=makeQuery(id+"F20.imprint","IMPRINT",FACE,{"disambiguationData":[TD([[makeQuery(id+"F20.imprint","IMPRINT",EDGE,{"derivedFrom":sQuery(id+"F20.wireOp",EDGE,"E61")}),-1.0]])]});
            var Q3;
            {var subQ0=sQuery(id+"F20.wireOp",EDGE,"E78.2.0");Q3=makeQuery(id+"F20.imprint","IMPRINT",FACE,{"disambiguationData":[TD([[makeQuery(id+"F20.imprint","IMPRINT",EDGE,{"derivedFrom":subQ0}),1.0]])]});}
            var Q4;
            {var subQ0=sQuery(id+"F20.wireOp",EDGE,"E78.1.0");Q4=makeQuery(id+"F20.imprint","IMPRINT",FACE,{"disambiguationData":[TD([[makeQuery(id+"F20.imprint","IMPRINT",EDGE,{"derivedFrom":subQ0}),1.0]])]});}
            var Q5;
            Q5=makeQuery(id+"F20.imprint","IMPRINT",FACE,{"disambiguationData":[TD([[makeQuery(id+"F20.imprint","IMPRINT",EDGE,{"derivedFrom":sQuery(id+"F20.wireOp",EDGE,"E63.1.0")}),-1.0]])]});
            var Q6;
            Q6=makeQuery(id+"F20.imprint","IMPRINT",FACE,{"disambiguationData":[TD([[makeQuery(id+"F20.imprint","IMPRINT",EDGE,{"derivedFrom":sQuery(id+"F20.wireOp",EDGE,"E63.2.0")}),-1.0]])]});
            var Q7;
            {var subQ2=sQuery(id+"F20.wireOp",EDGE,"E85.1.0");Q7=makeQuery(id+"F20.imprint","IMPRINT",FACE,{"disambiguationData":[TD([[makeQuery(id+"F20.imprint","IMPRINT",EDGE,{"derivedFrom":subQ2}),1.0]])]});}
            var Q8;
            {var subQ0=sQuery(id+"F20.wireOp",EDGE,"E82");Q8=makeQuery(id+"F20.imprint","IMPRINT",FACE,{"disambiguationData":[TD([[makeQuery(id+"F20.imprint","IMPRINT",EDGE,{"derivedFrom":subQ0}),1.0]])]});}
            var Q9;
            {var subQ2=sQuery(id+"F20.wireOp",EDGE,"E85.2.0");Q9=makeQuery(id+"F20.imprint","IMPRINT",FACE,{"disambiguationData":[TD([[makeQuery(id+"F20.imprint","IMPRINT",EDGE,{"derivedFrom":subQ2}),1.0]])]});}
            extrude(context, id + "F21", {"entities" : qUnion([Q0, Q1, Q2, Q3, Q4, Q5, Q6, Q7, Q8, Q9]), "depth" : 5 * mm, "offsetDistance" : 25 * mm});
        }
    });
